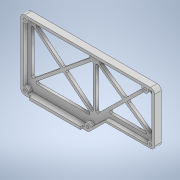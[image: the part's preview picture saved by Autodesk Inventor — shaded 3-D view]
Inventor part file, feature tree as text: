
AUTODESK INVENTOR PART (.ipt)
format: ipt  version: 2021 (Build 250183000, 183)  size: 491,008 bytes
history: native  units: mm
features: sketch x18, extrude x16, fillet x5, hole x2, chamfer x2
ambient origin geometry x8: Origin, YZ Plane, XZ Plane, XY Plane, X Axis, Y Axis, Z Axis, Center Point
bodies: Solid1 (feature_tree)
feature tree (43):
  extrude  "Extrusion1"  Depth=100.0mm
  extrude  "Extrusion2"  Depth=50.0mm
  hole  "Hole1"  [1 undecoded]
  extrude  "Extrusion3"  Depth=50.0mm
  extrude  "Extrusion4"  Depth=3.0mm
  extrude  "Extrusion5"  Depth=3.0mm
  fillet  "Fillet1"  Radius=49.0mm
  extrude  "Extrusion6"  Depth=93.0mm
  extrude  "Extrusion7"  Depth=5.0mm
  extrude  "Extrusion8"  Depth=5.0mm
  chamfer  "Chamfer1"  Distance=3.0mm
  extrude  "Extrusion9"  Depth=12.5mm
  fillet  "Fillet2"  Radius=63.1mm
  extrude  "Extrusion11"  Depth=3.0mm
  extrude  "Extrusion12"  Depth=2.0mm
  chamfer  "Chamfer2"  Distance=2.0mm
  extrude  "Extrusion13"  Depth=2.0mm
  extrude  "Extrusion14"  Depth=1.5mm
  extrude  "Extrusion15"  Depth=3.0mm TaperAngle=0.0deg
  fillet  "Fillet3"  Radius=3.0mm
  fillet  "Fillet4"  Radius=7.6mm
  hole  "Hole2"  [1 undecoded]
  extrude  "Extrusion20"  Depth=3.0mm
  extrude  "Extrusion21"  Depth=3.0mm TaperAngle=0.0deg
  fillet  "Fillet5"  Radius=5.0mm
  sketch  "Sketch1"  dims[d0=52.0mm d1=100.0mm]
  sketch  "Sketch2"  dims[d2=26.0mm d3=50.0mm]
  sketch  "Sketch3"  dims[d4=2.0mm d5=0.0mm d6=3.0mm]
  sketch  "Sketch4"  dims[d7=3.0mm d8=50.0mm]
  sketch  "Sketch5"  dims[d9=3.0mm d10=97.0mm]
  sketch  "Sketch6"  dims[d11=15.0mm d12=3.0mm d13=49.0mm]
  sketch  "Sketch7"  dims[d14=93.0mm d15=49.0mm]
  sketch  "Sketch8"  dims[d16=2.0mm d17=5.0mm]
  sketch  "Sketch9"  dims[d18=2.0mm d19=5.0mm]
  sketch  "Sketch10"  dims[d20=2.0mm]
  sketch  "Sketch12"  dims[d21=5.0mm]
  sketch  "Sketch13"  dims[d22=2.0mm]
  sketch  "Sketch14"  dims[d23=5.0mm]
  sketch  "Sketch15"  dims[d24=2.0mm]
  sketch  "Sketch16"  dims[d25=5.0mm d26=3.0mm d27=0.0mm]
  sketch  "Sketch17"  dims[d28=2.0mm d29=6.0mm d30=5.0mm d31=2.0mm d32=90.0deg d33=10.0mm d34=20.594885mm d35=12.5mm d36=63.1mm]
  sketch  "Sketch23"  dims[d37=3.0mm d38=0.0mm d39=50.673mm]
  sketch  "Sketch24"  dims[d40=3.0mm d41=0.0mm d42=2.0mm d43=2.0mm d44=2.0mm d45=1.5mm d46=3.0mm d47=0.0mm d48=3.0mm d49=7.6mm d50=46.4mm d51=6.7mm d52=3.0mm d53=0.0mm d54=5.0mm d55=2.0mm d56=12.0mm d57=0.0mm d58=1.4mm d59=1.2mm d60=3.0mm d61=14.0mm d62=1.2mm d63=1.4mm d64=12.0mm d65=3.0mm d66=0.0mm d67=1.0mm d68=2.0mm d69=45.0deg d70=1.2mm d71=3.0mm d72=0.0mm d73=1.0mm d77=3.0mm d78=0.0mm d79=3.0mm d80=3.0mm d81=3.0mm d82=3.0mm d83=3.0mm d84=3.0mm d85=3.0mm d86=48.0mm d87=2.0mm d88=0.0mm d89=8.4mm d90=2.0mm d91=45.0deg d92=1.2mm d93=3.0mm d94=0.0mm d95=7.6mm d96=5.0mm d97=0.0mm d98=2.0mm d99=2.0mm d100=2.0mm d101=2.0mm d102=2.0mm d103=2.0mm d104=0.0mm d105=1.0mm d106=1.0mm d107=2.0mm d108=6.0mm d109=5.0mm d110=2.0mm d111=90.0deg d112=4.0mm d113=20.594885mm d146=6.5mm d147=5.0mm d148=2.0mm d149=0.0mm d150=0.3mm d151=0.3mm d152=2.0mm d153=0.0mm d154=3.0mm d74=0.872665mm d75=0.872665mm d76=0.5mm d114=0.75mm d115=20.594885mm d116=0.0625mm d117=0.75mm d118=0.375mm]
note: 2 required parameter values undecoded (feature->parameter linkage not recoverable at this tier; creation-order binding heuristic only, values carry confidence <= 0.55)
